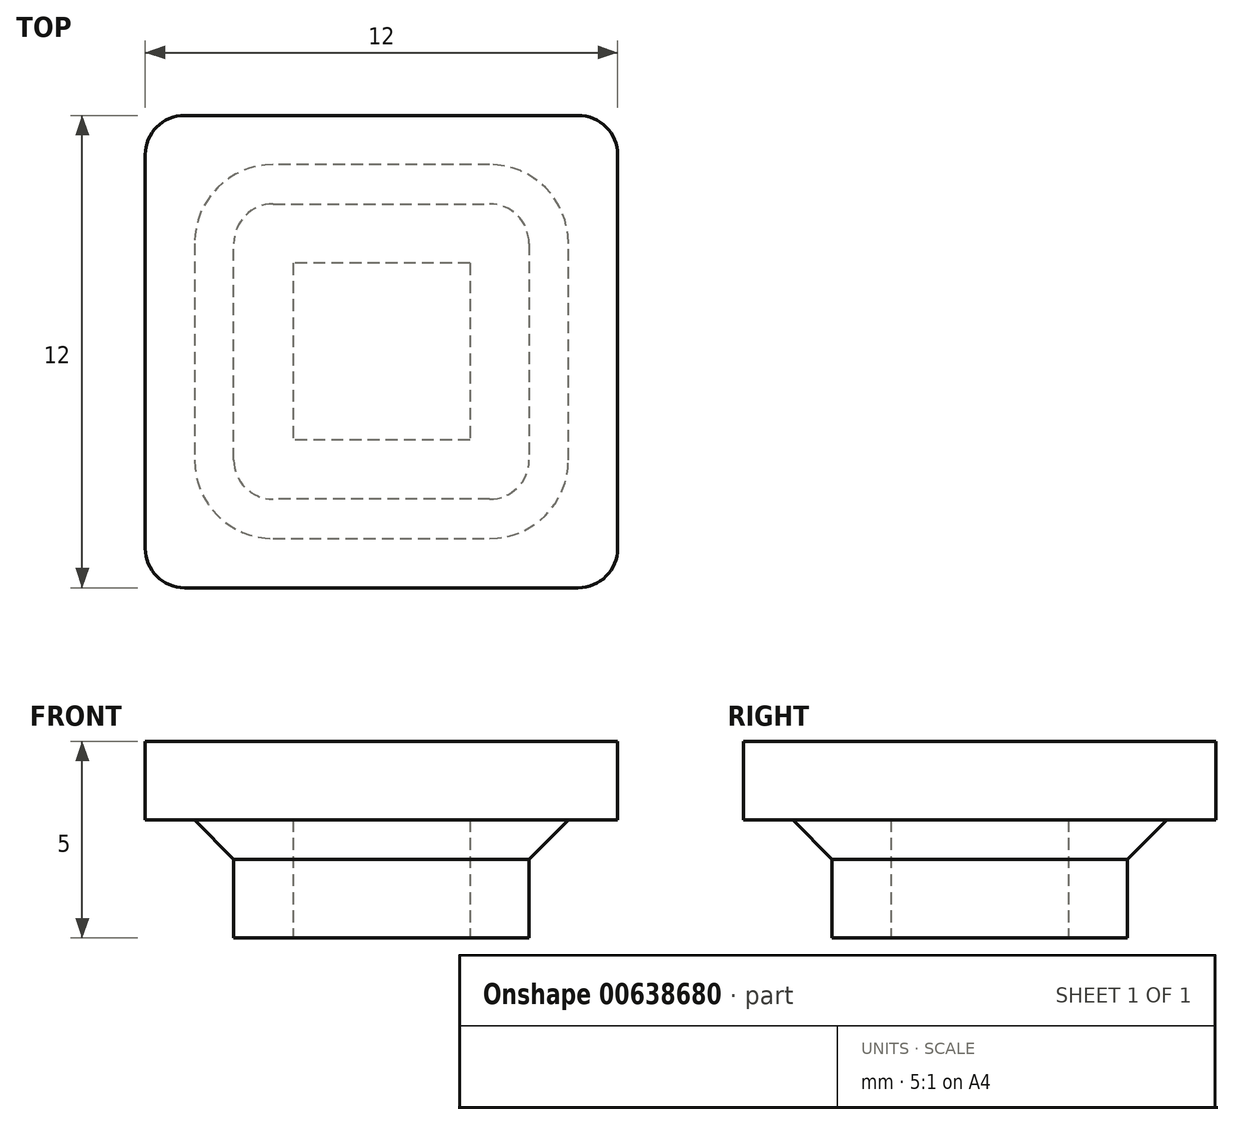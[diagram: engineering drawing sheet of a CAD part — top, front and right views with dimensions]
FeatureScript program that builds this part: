
annotation { "Feature Type Name" : "Feature", "Feature Type Description" : "" }
export const myFeature = defineFeature(function(context is Context, id is Id, definition is map)
    precondition{}
    {
        {
            var Q0;
            Q0=qCreatedBy(makeId("Top.planeOp"),FACE);
            var sketch = newSketch(context, id + "F0", { "sketchPlane" : qUnion([Q0])});
            skLineSegment(sketch, "E0.bottom", {"start": v(2.25, 2.25) * mm, "end": v(-2.25, 2.25) * mm});
            skLineSegment(sketch, "E0.top", {"start": v(2.25, -2.25) * mm, "end": v(-2.25, -2.25) * mm});
            skLineSegment(sketch, "E0.left", {"start": v(2.25, 2.25) * mm, "end": v(2.25, -2.25) * mm});
            skLineSegment(sketch, "E0.right", {"start": v(-2.25, 2.25) * mm, "end": v(-2.25, -2.25) * mm});
            skPoint(sketch, "E0.middle", {"position": v(0, 0) * mm});
            skLineSegment(sketch, "E1.0", {"start": v(2.75, -3.75) * mm, "end": v(-2.75, -3.75) * mm});
            skLineSegment(sketch, "E1.1", {"start": v(3.75, 2.75) * mm, "end": v(3.75, -2.75) * mm});
            skLineSegment(sketch, "E1.2", {"start": v(2.75, 3.75) * mm, "end": v(-2.75, 3.75) * mm});
            skLineSegment(sketch, "E1.3", {"start": v(-3.75, 2.75) * mm, "end": v(-3.75, -2.75) * mm});
            skPoint(sketch, "E2.visualSharp", {"position": v(3.75, 3.75) * mm});
            skArc(sketch, "E2.filletArc", {"start": v(3.75, 2.75) * mm, "mid": v(3.46, 3.46) * mm, "end": v(2.75, 3.75) * mm});
            skPoint(sketch, "E3.visualSharp", {"position": v(3.75, -3.75) * mm});
            skArc(sketch, "E3.filletArc", {"start": v(2.75, -3.75) * mm, "mid": v(3.46, -3.46) * mm, "end": v(3.75, -2.75) * mm});
            skPoint(sketch, "E4.visualSharp", {"position": v(-3.75, -3.75) * mm});
            skArc(sketch, "E4.filletArc", {"start": v(-3.75, -2.75) * mm, "mid": v(-3.46, -3.46) * mm, "end": v(-2.75, -3.75) * mm});
            skPoint(sketch, "E5.visualSharp", {"position": v(-3.75, 3.75) * mm});
            skArc(sketch, "E5.filletArc", {"start": v(-2.75, 3.75) * mm, "mid": v(-3.46, 3.46) * mm, "end": v(-3.75, 2.75) * mm});
            skSolve(sketch);
        }
        {
            var Q0;
            Q0 = qSketchRegion(id + "F0", true);
            extrude(context, id + "F1", {"entities" : qUnion([Q0]), "depth" : 3 * mm, "offsetDistance" : 25 * mm});
        }
        {
            var Q0;
            Q0=makeQuery(id+"F1.opExtrude","CAP_FACE",FACE,{"disambiguationData":[OSD([sQuery(id+"F0.wireOp",EDGE,"E0.bottom"),sQuery(id+"F0.wireOp",EDGE,"E0.top"),sQuery(id+"F0.wireOp",EDGE,"E0.left"),sQuery(id+"F0.wireOp",EDGE,"E0.right"),sQuery(id+"F0.wireOp",EDGE,"E1.0"),sQuery(id+"F0.wireOp",EDGE,"E1.1"),sQuery(id+"F0.wireOp",EDGE,"E1.2"),sQuery(id+"F0.wireOp",EDGE,"E1.3"),sQuery(id+"F0.wireOp",EDGE,"E2.filletArc"),sQuery(id+"F0.wireOp",EDGE,"E3.filletArc"),sQuery(id+"F0.wireOp",EDGE,"E4.filletArc"),sQuery(id+"F0.wireOp",EDGE,"E5.filletArc")])],"isStart":false});
            var sketch = newSketch(context, id + "F2", { "sketchPlane" : qUnion([Q0])});
            skLineSegment(sketch, "E6.bottom", {"start": v(5, 6) * mm, "end": v(-5, 6) * mm});
            skLineSegment(sketch, "E6.top", {"start": v(5, -6) * mm, "end": v(-5, -6) * mm});
            skLineSegment(sketch, "E6.left", {"start": v(6, 5) * mm, "end": v(6, -5) * mm});
            skLineSegment(sketch, "E6.right", {"start": v(-6, 5) * mm, "end": v(-6, -5) * mm});
            skPoint(sketch, "E6.middle", {"position": v(0, 0) * mm});
            skPoint(sketch, "E7.visualSharp", {"position": v(-6, 6) * mm});
            skArc(sketch, "E7.filletArc", {"start": v(-5, 6) * mm, "mid": v(-5.7, 5.7) * mm, "end": v(-6, 5) * mm});
            skPoint(sketch, "E8.visualSharp", {"position": v(-6, -6) * mm});
            skArc(sketch, "E8.filletArc", {"start": v(-6, -5) * mm, "mid": v(-5.7, -5.7) * mm, "end": v(-5, -6) * mm});
            skPoint(sketch, "E9.visualSharp", {"position": v(6, -6) * mm});
            skArc(sketch, "E9.filletArc", {"start": v(5, -6) * mm, "mid": v(5.7, -5.7) * mm, "end": v(6, -5) * mm});
            skPoint(sketch, "E10.visualSharp", {"position": v(6, 6) * mm});
            skArc(sketch, "E10.filletArc", {"start": v(6, 5) * mm, "mid": v(5.7, 5.7) * mm, "end": v(5, 6) * mm});
            skSolve(sketch);
        }
        {
            var Q0;
            Q0 = qSketchRegion(id + "F2", true);
            extrude(context, id + "F3", {"entities" : qUnion([Q0]), "operationType" : NewBodyOperationType.ADD, "depth" : 2 * mm, "offsetDistance" : 25 * mm});
        }
        {
            var Q0;
            Q0=makeQuery(id+"F1.opExtrude","CAP_EDGE",EDGE,{"disambiguationData":[OSD([sQuery(id+"F0.wireOp",EDGE,"E1.0")])],"isStart":false});
            chamfer(context, id + "F4", {"entities" : qUnion([Q0]), "width" : 1 * mm, "tangentPropagation" : true});
        }
    });
